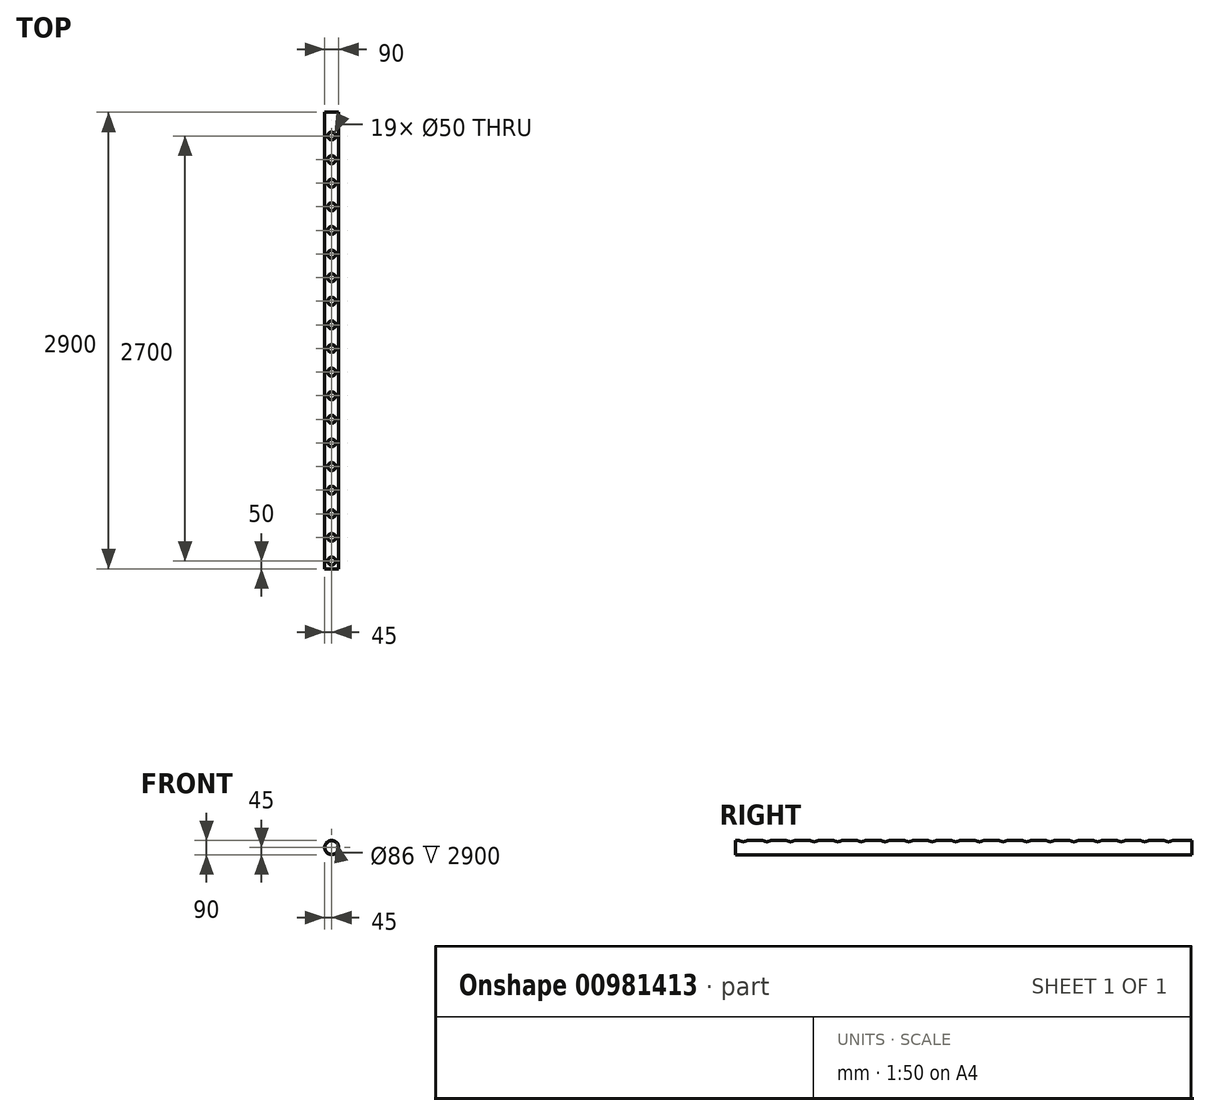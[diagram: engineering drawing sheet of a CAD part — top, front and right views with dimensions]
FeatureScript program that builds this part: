
annotation { "Feature Type Name" : "Feature", "Feature Type Description" : "" }
export const myFeature = defineFeature(function(context is Context, id is Id, definition is map)
    precondition{}
    {
        {
            var Q0;
            Q0=qCreatedBy(makeId("Front.planeOp"),FACE);
            var sketch = newSketch(context, id + "F0", { "sketchPlane" : qUnion([Q0])});
            skCircle(sketch, "E0", {"center": v(0, 0) * mm, "radius": 45 * mm});
            skCircle(sketch, "E1.0", {"center": v(0, 0) * mm, "radius": 43 * mm});
            skSolve(sketch);
        }
        {
            var Q0;
            Q0=qSketchRegion(id+"F0",true);
            extrude(context, id + "F1", {"entities" : qUnion([Q0]), "endBound" : BoundingType.SYMMETRIC, "depth" : 2900 * mm, "offsetDistance" : 25 * mm});
        }
        {
            var Q0;
            Q0=qCreatedBy(makeId("Top.planeOp"),FACE);
            cPlane(context, id + "F2", {"entities" : qUnion([Q0]), "cplaneType" : CPlaneType.OFFSET, "offset" : 45 * mm, "width" : 150 * mm, "height" : 150 * mm});
        }
        {
            var Q0;
            Q0=qCreatedBy(id+"F2.planeOp",FACE);
            var sketch = newSketch(context, id + "F3", { "sketchPlane" : qUnion([Q0])});
            skPoint(sketch, "E2", {"position": v(0, -1400) * mm});
            skPoint(sketch, "E3", {"position": v(0, -1250) * mm});
            skPoint(sketch, "E4", {"position": v(0, -1100) * mm});
            skPoint(sketch, "E5", {"position": v(0, -950) * mm});
            skPoint(sketch, "E6", {"position": v(0, -800) * mm});
            skPoint(sketch, "E7", {"position": v(0, -650) * mm});
            skPoint(sketch, "E8", {"position": v(0, -500) * mm});
            skPoint(sketch, "E9", {"position": v(0, -350) * mm});
            skPoint(sketch, "E10", {"position": v(0, -200) * mm});
            skPoint(sketch, "E11", {"position": v(0, -50) * mm});
            skPoint(sketch, "E12", {"position": v(0, 100) * mm});
            skPoint(sketch, "E13", {"position": v(0, 250) * mm});
            skPoint(sketch, "E14", {"position": v(0, 400) * mm});
            skPoint(sketch, "E15", {"position": v(0, 550) * mm});
            skPoint(sketch, "E16", {"position": v(0, 700) * mm});
            skPoint(sketch, "E17", {"position": v(0, 850) * mm});
            skPoint(sketch, "E18", {"position": v(0, 1000) * mm});
            skPoint(sketch, "E19", {"position": v(0, 1150) * mm});
            skPoint(sketch, "E20", {"position": v(0, 1300) * mm});
            skSolve(sketch);
        }
        {
            var Q0;
            Q0=sQuery(id+"F3.wireOp",VERTEX,"E2");
            var Q1;
            Q1=sQuery(id+"F3.wireOp",VERTEX,"E3");
            var Q2;
            Q2=sQuery(id+"F3.wireOp",VERTEX,"E4");
            var Q3;
            Q3=sQuery(id+"F3.wireOp",VERTEX,"E5");
            var Q4;
            Q4=sQuery(id+"F3.wireOp",VERTEX,"E6");
            var Q5;
            Q5=sQuery(id+"F3.wireOp",VERTEX,"E7");
            var Q6;
            Q6=sQuery(id+"F3.wireOp",VERTEX,"E8");
            var Q7;
            Q7=sQuery(id+"F3.wireOp",VERTEX,"E9");
            var Q8;
            Q8=sQuery(id+"F3.wireOp",VERTEX,"E10");
            var Q9;
            Q9=sQuery(id+"F3.wireOp",VERTEX,"E11");
            var Q10;
            Q10=sQuery(id+"F3.wireOp",VERTEX,"E12");
            var Q11;
            Q11=sQuery(id+"F3.wireOp",VERTEX,"E13");
            var Q12;
            Q12=sQuery(id+"F3.wireOp",VERTEX,"E14");
            var Q13;
            Q13=sQuery(id+"F3.wireOp",VERTEX,"E15");
            var Q14;
            Q14=sQuery(id+"F3.wireOp",VERTEX,"E16");
            var Q15;
            Q15=sQuery(id+"F3.wireOp",VERTEX,"E17");
            var Q16;
            Q16=sQuery(id+"F3.wireOp",VERTEX,"E18");
            var Q17;
            Q17=sQuery(id+"F3.wireOp",VERTEX,"E19");
            var Q18;
            Q18=sQuery(id+"F3.wireOp",VERTEX,"E20");
            var Q19;
            Q19=sQuery(id+"F3.wireOp",VERTEX,"4217ffee-23aa-4e57-b56b-1031955cdd20");
            var Q20;
            Q20=sQuery(id+"F3.wireOp",VERTEX,"f9e667d2-43f0-46cb-85dd-7700daad2ab1");
            var Q21;
            Q21=sQuery(id+"F3.wireOp",VERTEX,"a141cc4f-d6fa-4136-a428-d91cc8b08e23");
            var Q22;
            Q22=sQuery(id+"F3.wireOp",VERTEX,"6950c5e6-caf7-4953-8c5b-56709a9cffe9");
            var Q23;
            Q23=sQuery(id+"F3.wireOp",VERTEX,"1581daf2-9304-4365-a3cc-e960652a3bf4");
            var Q24;
            Q24=sQuery(id+"F3.wireOp",VERTEX,"25a0b738-50ad-46bb-ba52-db4eb22869ea");
            var Q25;
            Q25=sQuery(id+"F3.wireOp",VERTEX,"23c6b068-1da5-4682-a93c-07f6e733a235");
            var Q26;
            Q26=sQuery(id+"F3.wireOp",VERTEX,"77491461-51bd-4097-a69a-b50156a0fef7");
            var Q27;
            Q27=sQuery(id+"F3.wireOp",VERTEX,"89e2eaf9-af87-4198-a739-5b01357332c3");
            var Q28;
            Q28=sQuery(id+"F3.wireOp",VERTEX,"a31ac070-19d1-4092-b391-6f630edb761b");
            var Q29;
            Q29=makeQuery(id+"F1.opExtrude","SWEPT_BODY",BODY,{"disambiguationData":[OSD([sQuery(id+"F0.wireOp",EDGE,"E0"),sQuery(id+"F0.wireOp",EDGE,"E1.0")])]});
            hole(context, id + "F4", {"style" : HoleStyle.SIMPLE, "endStyle" : HoleEndStyle.BLIND, "holeDiameter" : 50 * mm, "majorDiameter" : 5 * mm, "holeDepth" : 50 * mm, "isTappedThrough" : true, "tappedDepth" : 12 * mm, "tapClearance" : 3, "startFromSketch" : true, "locations" : qUnion([Q0, Q1, Q2, Q3, Q4, Q5, Q6, Q7, Q8, Q9, Q10, Q11, Q12, Q13, Q14, Q15, Q16, Q17, Q18, Q19, Q20, Q21, Q22, Q23, Q24, Q25, Q26, Q27, Q28]), "scope" : qUnion([Q29])});
        }
    });
